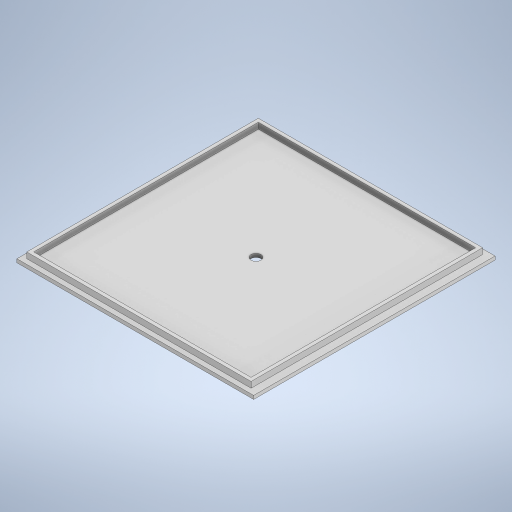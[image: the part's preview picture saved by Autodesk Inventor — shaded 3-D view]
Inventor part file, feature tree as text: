
AUTODESK INVENTOR PART (.ipt)
format: ipt  version: 2024 (Build 280153000, 153)  size: 246,272 bytes
history: native  units: mm
features: extrude x3, sketch x2
ambient origin geometry x8: Origin, YZ Plane, XZ Plane, XY Plane, X Axis, Y Axis, Z Axis, Center Point
bodies: Solid1 (feature_tree)
feature tree (5):
  sketch  "Sketch1"  dims[d0=101.0mm d1=103.0mm]
  extrude  "Extrusion1"  Depth=103.0mm
  extrude  "Extrusion2"  Depth=3.2mm
  extrude  "Extrusion3"  Depth=1.5mm
  sketch  "Sketch2"  dims[d2=2.1mm d3=3.2mm d4=1.5mm d5=1.5mm d6=0.0mm d7=4.0mm d8=0.0mm d9=4.2mm d10=4.0mm d11=0.0mm]
